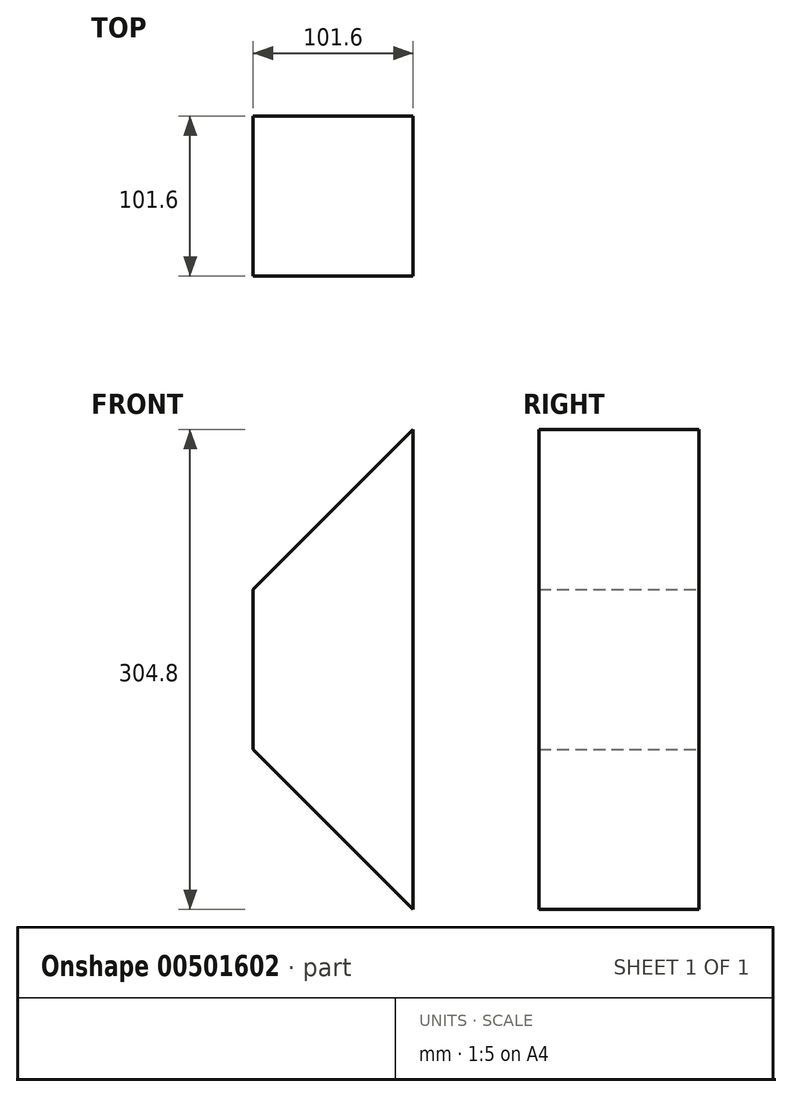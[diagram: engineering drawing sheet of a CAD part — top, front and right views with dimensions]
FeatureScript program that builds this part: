
annotation { "Feature Type Name" : "Feature", "Feature Type Description" : "" }
export const myFeature = defineFeature(function(context is Context, id is Id, definition is map)
    precondition{}
    {
        {
            var Q0;
            Q0=qCreatedBy(makeId("Front.planeOp"),FACE);
            var sketch = newSketch(context, id + "F0", { "sketchPlane" : qUnion([Q0])});
            skLineSegment(sketch, "E0.bottom", {"start": v(50.8, 1219.2) * mm, "end": v(-50.8, 1219.2) * mm});
            skLineSegment(sketch, "E0.top", {"start": v(50.8, -1219.2) * mm, "end": v(-50.8, -1219.2) * mm});
            skLineSegment(sketch, "E0.left", {"start": v(50.8, 1219.2) * mm, "end": v(50.8, -1219.2) * mm});
            skLineSegment(sketch, "E0.right", {"start": v(-50.8, 1219.2) * mm, "end": v(-50.8, -1219.2) * mm});
            skPoint(sketch, "E0.middle", {"position": v(0, 0) * mm});
            skLineSegment(sketch, "E1", {"start": v(-50.8, 1219.2) * mm, "end": v(50.8, 1117.6) * mm});
            skLineSegment(sketch, "E2", {"start": v(-50.8, 914.4) * mm, "end": v(50.8, 1016) * mm});
            skLineSegment(sketch, "E3", {"start": v(-50.8, 812.8) * mm, "end": v(50.8, 711.2) * mm});
            skSolve(sketch);
        }
        {
            var Q0;
            {var subQ0=sQuery(id+"F0.wireOp",EDGE,"E2");Q0=makeQuery(id+"F0.imprint","IMPRINT",FACE,{"disambiguationData":[TD([[makeQuery(id+"F0.imprint","IMPRINT",EDGE,{"derivedFrom":subQ0}),-1.0]])]});}
            extrude(context, id + "F1", {"entities" : qUnion([Q0]), "depth" : 101.6 * mm, "offsetDistance" : 25.4 * mm});
        }
    });
